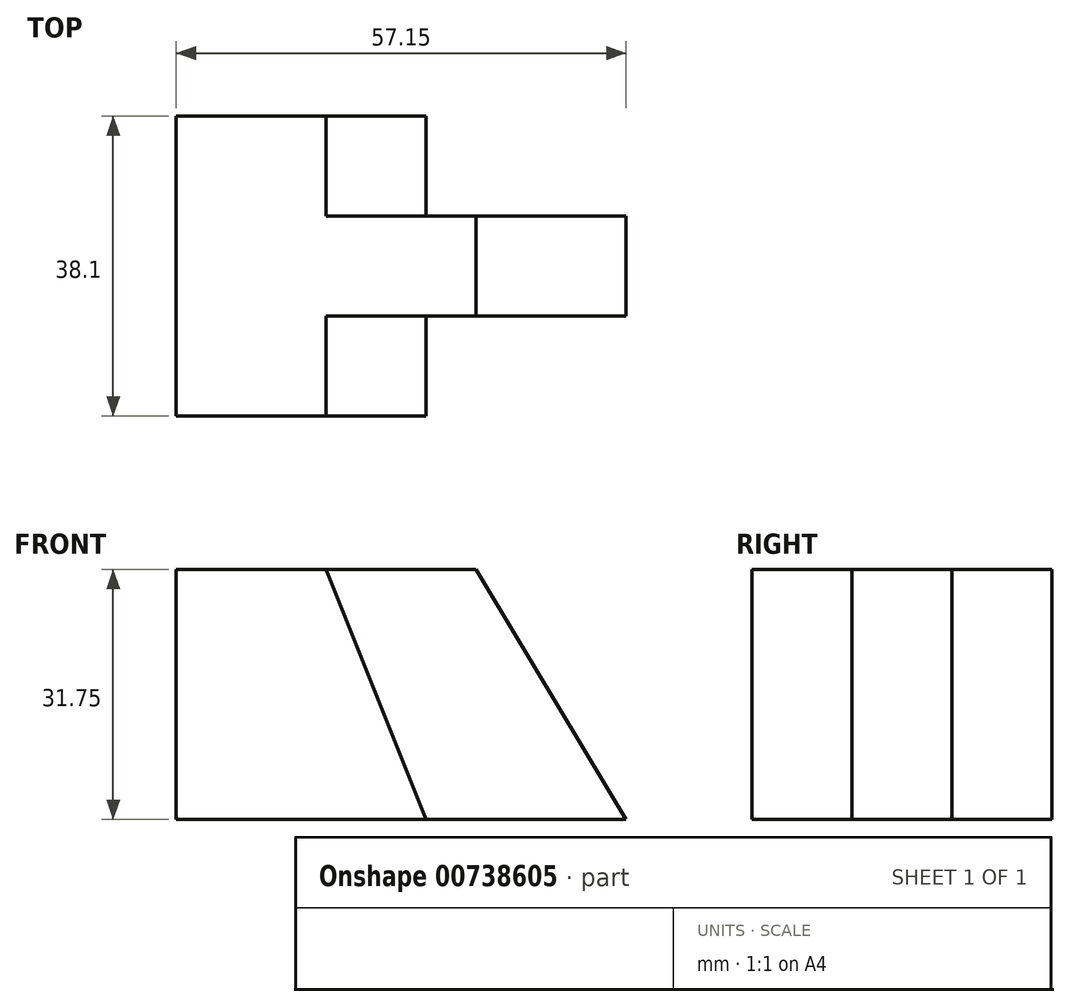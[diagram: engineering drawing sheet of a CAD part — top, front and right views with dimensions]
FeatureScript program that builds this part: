
annotation { "Feature Type Name" : "Feature", "Feature Type Description" : "" }
export const myFeature = defineFeature(function(context is Context, id is Id, definition is map)
    precondition{}
    {
        {
            var Q0;
            Q0=qCreatedBy(makeId("Front.planeOp"),FACE);
            var sketch = newSketch(context, id + "F0", { "sketchPlane" : qUnion([Q0])});
            skLineSegment(sketch, "E0", {"start": v(0, 31.75) * mm, "end": v(0, 0) * mm});
            skLineSegment(sketch, "E1", {"start": v(0, 0) * mm, "end": v(57.15, 0) * mm});
            skLineSegment(sketch, "E2", {"start": v(57.15, 0) * mm, "end": v(57.15, 31.75) * mm});
            skLineSegment(sketch, "E3", {"start": v(57.15, 31.75) * mm, "end": v(0, 31.75) * mm});
            skSolve(sketch);
        }
        {
            var Q0;
            Q0 = qSketchRegion(id + "F0", true);
            extrude(context, id + "F1", {"entities" : qUnion([Q0]), "depth" : 38.1 * mm, "offsetDistance" : 25.4 * mm});
        }
        {
            var Q0;
            Q0=makeQuery(id+"F1.opExtrude","CAP_FACE",FACE,{"disambiguationData":[OSD([sQuery(id+"F0.wireOp",EDGE,"E0"),sQuery(id+"F0.wireOp",EDGE,"E1"),sQuery(id+"F0.wireOp",EDGE,"E2"),sQuery(id+"F0.wireOp",EDGE,"E3")])],"isStart":false});
            var sketch = newSketch(context, id + "F2", { "sketchPlane" : qUnion([Q0])});
            skLineSegment(sketch, "E4", {"start": v(19.05, 31.75) * mm, "end": v(31.75, 0) * mm});
            skSolve(sketch);
        }
        {
            var Q0;
            {var subQ0=sQuery(id+"F2.wireOp",EDGE,"E4");Q0=makeQuery(id+"F2.imprint","IMPRINT",FACE,{"disambiguationData":[TD([[makeQuery(id+"F2.imprint","IMPRINT",EDGE,{"derivedFrom":subQ0}),1.0]])]});}
            extrude(context, id + "F3", {"entities" : qUnion([Q0]), "operationType" : NewBodyOperationType.REMOVE, "oppositeDirection" : true, "depth" : 12.7 * mm, "offsetDistance" : 25.4 * mm});
        }
        {
            var Q0;
            Q0=makeQuery(id+"F1.opExtrude","CAP_FACE",FACE,{"disambiguationData":[OSD([sQuery(id+"F0.wireOp",EDGE,"E0"),sQuery(id+"F0.wireOp",EDGE,"E1"),sQuery(id+"F0.wireOp",EDGE,"E2"),sQuery(id+"F0.wireOp",EDGE,"E3")])],"isStart":true});
            var sketch = newSketch(context, id + "F4", { "sketchPlane" : qUnion([Q0])});
            skLineSegment(sketch, "E5", {"start": v(-19.05, 31.75) * mm, "end": v(-31.75, 0) * mm});
            skSolve(sketch);
        }
        {
            var Q0;
            Q0 = qSketchRegion(id + "F4", true);
            var Q1;
            {var subQ0=sQuery(id+"F4.wireOp",EDGE,"E5");Q1=makeQuery(id+"F4.imprint","IMPRINT",FACE,{"disambiguationData":[TD([[makeQuery(id+"F4.imprint","IMPRINT",EDGE,{"derivedFrom":subQ0}),-1.0]])]});}
            extrude(context, id + "F5", {"entities" : qUnion([Q0, Q1]), "operationType" : NewBodyOperationType.REMOVE, "oppositeDirection" : true, "depth" : 12.7 * mm, "offsetDistance" : 25.4 * mm});
        }
        {
            var Q0;
            Q0=makeQuery(id+"F3.boolean.opBoolean","COPY",FACE,{"derivedFrom":makeQuery(id+"F3.opExtrude","CAP_FACE",FACE,{"disambiguationData":[OSD([sQuery(id+"F0.wireOp",EDGE,"E1"),sQuery(id+"F0.wireOp",EDGE,"E2"),sQuery(id+"F0.wireOp",EDGE,"E3"),sQuery(id+"F2.wireOp",EDGE,"E4")])],"isStart":false})});
            var sketch = newSketch(context, id + "F6", { "sketchPlane" : qUnion([Q0])});
            skLineSegment(sketch, "E6", {"start": v(57.15, 0) * mm, "end": v(38.1, 31.75) * mm});
            skSolve(sketch);
        }
        {
            var Q0;
            Q0 = qSketchRegion(id + "F6", true);
            var Q1;
            {var subQ0=sQuery(id+"F6.wireOp",EDGE,"E6");Q1=makeQuery(id+"F6.imprint","IMPRINT",FACE,{"disambiguationData":[TD([[makeQuery(id+"F6.imprint","IMPRINT",EDGE,{"derivedFrom":subQ0}),-1.0]])]});}
            extrude(context, id + "F7", {"entities" : qUnion([Q0, Q1]), "operationType" : NewBodyOperationType.REMOVE, "endBound" : BoundingType.THROUGH_ALL, "oppositeDirection" : true, "depth" : 25.4 * mm, "offsetDistance" : 25.4 * mm});
        }
    });
